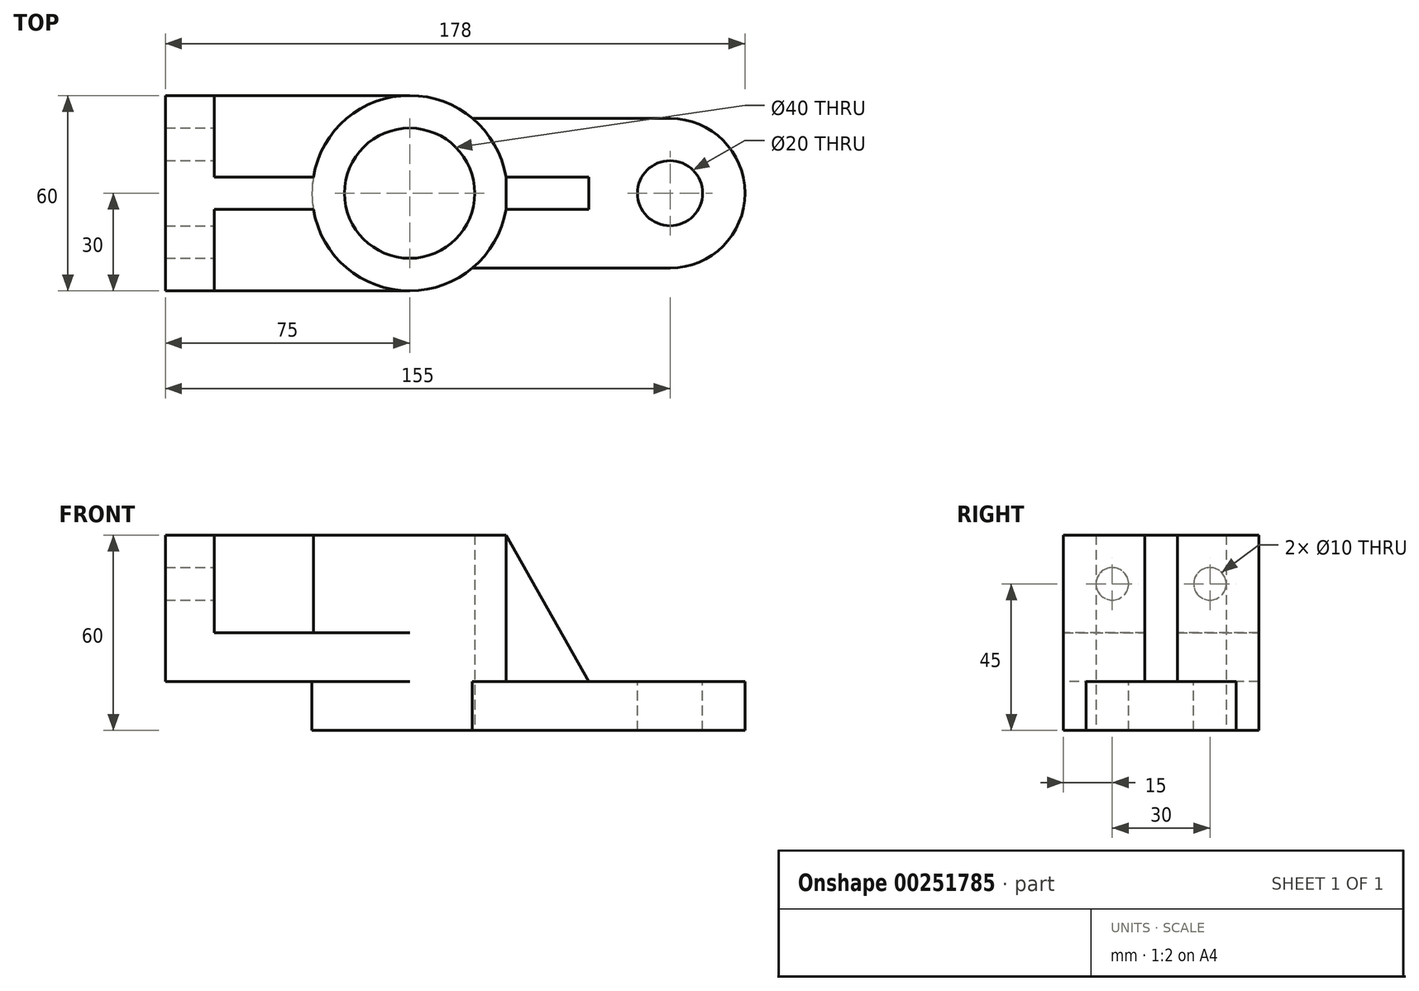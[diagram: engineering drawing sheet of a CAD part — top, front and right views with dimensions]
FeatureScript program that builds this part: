
annotation { "Feature Type Name" : "Feature", "Feature Type Description" : "" }
export const myFeature = defineFeature(function(context is Context, id is Id, definition is map)
    precondition{}
    {
        {
            var Q0;
            Q0=qCreatedBy(makeId("Top.planeOp"),FACE);
            var sketch = newSketch(context, id + "F0", { "sketchPlane" : qUnion([Q0])});
            skCircle(sketch, "E0", {"center": v(0, 0) * mm, "radius": 30 * mm});
            skCircle(sketch, "E1", {"center": v(0, 0) * mm, "radius": 20 * mm});
            skSolve(sketch);
        }
        {
            var Q0;
            Q0 = qSketchRegion(id + "F0", true);
            extrude(context, id + "F1", {"entities" : qUnion([Q0]), "endBound" : BoundingType.SYMMETRIC, "depth" : 60 * mm});
        }
        {
            var Q0;
            Q0=makeQuery(id+"F1.opExtrude","CAP_FACE",FACE,{"disambiguationData":[OSD([sQuery(id+"F0.wireOp",EDGE,"E0"),sQuery(id+"F0.wireOp",EDGE,"E1")])],"isStart":true});
            var sketch = newSketch(context, id + "F2", { "sketchPlane" : qUnion([Q0])});
            skLineSegment(sketch, "E2", {"start": v(80, 68.58) * mm, "end": v(80, -73.94) * mm});
            skLineSegment(sketch, "E3.bottom", {"start": v(19.26, 23) * mm, "end": v(80, 23) * mm});
            skLineSegment(sketch, "E3.top", {"start": v(19.26, -23) * mm, "end": v(80, -23) * mm});
            skCircle(sketch, "E4", {"center": v(80, 0) * mm, "radius": 23 * mm});
            skArc(sketch, "E5.0", {"start": v(19.26, -23) * mm, "mid": v(30, 0) * mm, "end": v(19.26, 23) * mm});
            skSolve(sketch);
        }
        {
            var Q0;
            Q0 = qSketchRegion(id + "F2", true);
            extrude(context, id + "F3", {"entities" : qUnion([Q0]), "operationType" : NewBodyOperationType.ADD, "oppositeDirection" : true, "depth" : 15 * mm});
        }
        {
            var Q0;
            Q0=makeQuery(id+"F3.opExtrude","CAP_FACE",FACE,{"disambiguationData":[OSD([sQuery(id+"F2.wireOp",EDGE,"E3.bottom"),sQuery(id+"F2.wireOp",EDGE,"E3.top"),sQuery(id+"F2.wireOp",EDGE,"E4"),sQuery(id+"F2.wireOp",EDGE,"E5.0")])],"isStart":false});
            var sketch = newSketch(context, id + "F4", { "sketchPlane" : qUnion([Q0])});
            skCircle(sketch, "E6", {"center": v(80, 0) * mm, "radius": 10 * mm});
            skSolve(sketch);
        }
        {
            var Q0;
            Q0 = qSketchRegion(id + "F4", true);
            extrude(context, id + "F5", {"entities" : qUnion([Q0]), "operationType" : NewBodyOperationType.REMOVE, "oppositeDirection" : true, "depth" : 25 * mm});
        }
        {
            var Q0;
            Q0=makeQuery(id+"F3.opExtrude","CAP_FACE",FACE,{"disambiguationData":[OSD([sQuery(id+"F2.wireOp",EDGE,"E3.bottom"),sQuery(id+"F2.wireOp",EDGE,"E3.top"),sQuery(id+"F2.wireOp",EDGE,"E4"),sQuery(id+"F2.wireOp",EDGE,"E5.0")])],"isStart":false});
            var sketch = newSketch(context, id + "F6", { "sketchPlane" : qUnion([Q0])});
            skPoint(sketch, "E7.oppositeSnap0", {"position": v(55, -5) * mm});
            skLineSegment(sketch, "E7.bottom", {"start": v(29.58, 5) * mm, "end": v(55, 5) * mm});
            skLineSegment(sketch, "E7.top", {"start": v(29.58, -5) * mm, "end": v(55, -5) * mm});
            skPoint(sketch, "E8.endSnap0", {"position": v(103, 0) * mm});
            skArc(sketch, "E9.0", {"start": v(29.58, -5) * mm, "mid": v(30, 0) * mm, "end": v(29.58, 5) * mm});
            skPoint(sketch, "E10.orphan", {"position": v(122.44, -5) * mm});
            skPoint(sketch, "E11.orphan", {"position": v(55, 104.08) * mm});
            skPoint(sketch, "E12.orphan", {"position": v(55, -114.08) * mm});
            skPoint(sketch, "E13.orphan", {"position": v(190.87, 0) * mm});
            skLineSegment(sketch, "E14", {"start": v(55, 5) * mm, "end": v(55, -5) * mm});
            skSolve(sketch);
        }
        {
            var Q0;
            Q0 = qSketchRegion(id + "F6", true);
            extrude(context, id + "F7", {"entities" : qUnion([Q0]), "operationType" : NewBodyOperationType.ADD, "depth" : 45 * mm});
        }
        {
            var Q0;
            Q0=makeQuery(id+"F7.opExtrude","SWEPT_FACE",FACE,{"disambiguationData":[OSD([sQuery(id+"F6.wireOp",EDGE,"E7.top")])]});
            var sketch = newSketch(context, id + "F8", { "sketchPlane" : qUnion([Q0])});
            skLineSegment(sketch, "E15", {"start": v(55, -15) * mm, "end": v(29.58, 30) * mm});
            skPoint(sketch, "E16.0", {"position": v(55, 30) * mm});
            skLineSegment(sketch, "E17.0", {"start": v(29.58, 30) * mm, "end": v(55, 30) * mm});
            skLineSegment(sketch, "E18.0", {"start": v(55, 30) * mm, "end": v(55, -15) * mm});
            skSolve(sketch);
        }
        {
            var Q0;
            Q0 = qSketchRegion(id + "F8", true);
            extrude(context, id + "F9", {"entities" : qUnion([Q0]), "operationType" : NewBodyOperationType.REMOVE, "endBound" : BoundingType.THROUGH_ALL, "oppositeDirection" : true, "depth" : 25 * mm});
        }
        {
            var Q0;
            Q0=qCreatedBy(makeId("Top.planeOp"),FACE);
            var sketch = newSketch(context, id + "F10", { "sketchPlane" : qUnion([Q0])});
            skLineSegment(sketch, "E19.bottom", {"start": v(0, 30) * mm, "end": v(-75, 30) * mm});
            skLineSegment(sketch, "E19.top", {"start": v(0, -30) * mm, "end": v(-75, -30) * mm});
            skLineSegment(sketch, "E19.right", {"start": v(-75, 30) * mm, "end": v(-75, -30) * mm});
            skPoint(sketch, "E19.middle", {"position": v(-37.5, 0) * mm});
            skArc(sketch, "E20.0", {"start": v(0, 30) * mm, "mid": v(-22.91, -19.36) * mm, "end": v(29.58, -5) * mm});
            skPoint(sketch, "E21.orphan", {"position": v(29.58, 5) * mm});
            skSolve(sketch);
        }
        {
            var Q0;
            Q0 = qSketchRegion(id + "F10", true);
            extrude(context, id + "F11", {"entities" : qUnion([Q0]), "operationType" : NewBodyOperationType.ADD, "oppositeDirection" : true, "depth" : 15 * mm});
        }
        {
            var Q0;
            Q0=qCreatedBy(makeId("Front.planeOp"),FACE);
            var sketch = newSketch(context, id + "F12", { "sketchPlane" : qUnion([Q0])});
            skLineSegment(sketch, "E22.bottom", {"start": v(-75, 0) * mm, "end": v(-60, 0) * mm});
            skLineSegment(sketch, "E22.top", {"start": v(-75, 30) * mm, "end": v(-60, 30) * mm});
            skLineSegment(sketch, "E22.left", {"start": v(-75, 0) * mm, "end": v(-75, 30) * mm});
            skLineSegment(sketch, "E22.right", {"start": v(-60, 0) * mm, "end": v(-60, 30) * mm});
            skSolve(sketch);
        }
        {
            var Q0;
            Q0 = qSketchRegion(id + "F12", true);
            extrude(context, id + "F13", {"entities" : qUnion([Q0]), "operationType" : NewBodyOperationType.ADD, "endBound" : BoundingType.SYMMETRIC, "depth" : 60 * mm});
        }
        {
            var Q0;
            Q0=qCreatedBy(makeId("Top.planeOp"),FACE);
            var sketch = newSketch(context, id + "F14", { "sketchPlane" : qUnion([Q0])});
            skLineSegment(sketch, "E23.bottom", {"start": v(-60, 5) * mm, "end": v(-29.58, 5) * mm});
            skLineSegment(sketch, "E23.top", {"start": v(-60, -5) * mm, "end": v(-29.58, -5) * mm});
            skLineSegment(sketch, "E23.left", {"start": v(-60, 5) * mm, "end": v(-60, -5) * mm});
            skArc(sketch, "E24.0", {"start": v(-29.58, 5) * mm, "mid": v(-30, 0) * mm, "end": v(-29.58, -5) * mm});
            skPoint(sketch, "E25.orphan", {"position": v(29.58, 5) * mm});
            skPoint(sketch, "E26.orphan", {"position": v(29.58, -5) * mm});
            skSolve(sketch);
        }
        {
            var Q0;
            Q0 = qSketchRegion(id + "F14", true);
            extrude(context, id + "F15", {"entities" : qUnion([Q0]), "operationType" : NewBodyOperationType.ADD, "depth" : 30 * mm});
        }
        {
            var Q0;
            {var subQ0=sQuery(id+"F10.wireOp",EDGE,"E19.top");var subQ3=sQuery(id+"F12.wireOp",EDGE,"E22.right");Q0=makeQuery(id+"F15.boolean.opBoolean","SPLIT",FACE,{"disambiguationData":[TD([makeQuery(id+"F11.opExtrude","SWEPT_FACE",FACE,{"disambiguationData":[OSD([subQ0])]})])],"derivedFrom":makeQuery(id+"F13.opExtrude","SWEPT_FACE",FACE,{"disambiguationData":[OSD([subQ3])]})});}
            var sketch = newSketch(context, id + "F16", { "sketchPlane" : qUnion([Q0])});
            skLineSegment(sketch, "E27", {"start": v(0, 53.54) * mm, "end": v(0, -68.55) * mm, "construction": true});
            skLineSegment(sketch, "E28", {"start": v(49.96, 0) * mm, "end": v(-69.59, 0) * mm, "construction": true});
            skPoint(sketch, "E28.endSnap0", {"position": v(-17.5, 0) * mm});
            skCircle(sketch, "E29", {"center": v(-15, 15) * mm, "radius": 5 * mm});
            skCircle(sketch, "E30", {"center": v(15, 15) * mm, "radius": 5 * mm});
            skSolve(sketch);
        }
        {
            var Q0;
            Q0 = qSketchRegion(id + "F16", true);
            extrude(context, id + "F17", {"entities" : qUnion([Q0]), "operationType" : NewBodyOperationType.REMOVE, "endBound" : BoundingType.THROUGH_ALL, "oppositeDirection" : true, "depth" : 25 * mm});
        }
    });
